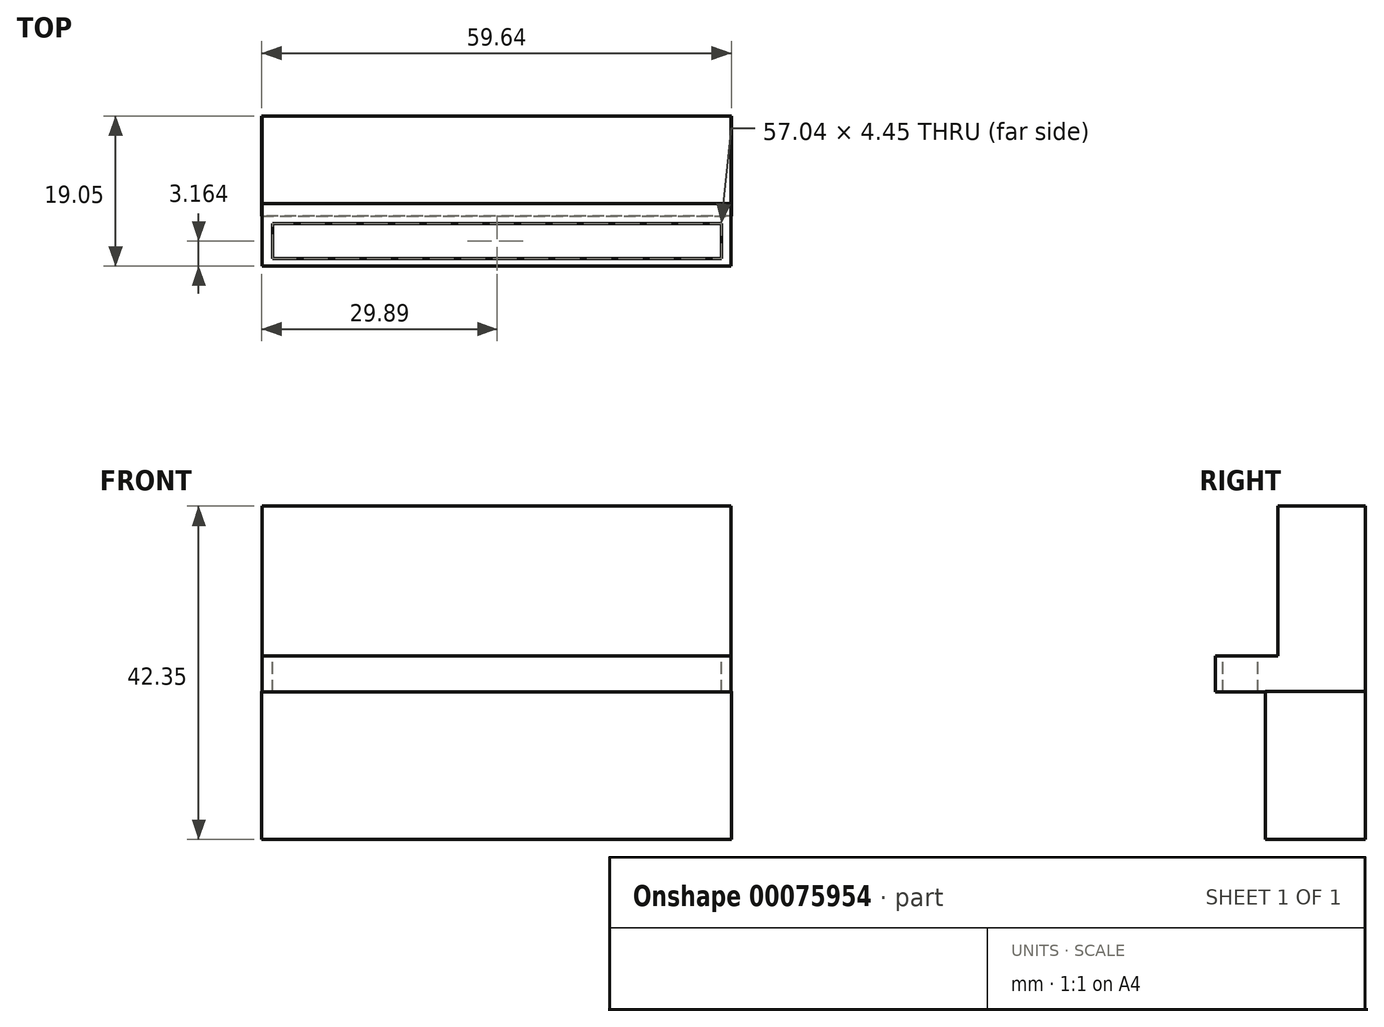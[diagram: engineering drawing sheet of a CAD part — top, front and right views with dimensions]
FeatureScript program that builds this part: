
annotation { "Feature Type Name" : "Feature", "Feature Type Description" : "" }
export const myFeature = defineFeature(function(context is Context, id is Id, definition is map)
    precondition{}
    {
        {
            var Q0;
            Q0=qCreatedBy(makeId("Front.planeOp"),FACE);
            var sketch = newSketch(context, id + "F0", { "sketchPlane" : qUnion([Q0])});
            skLineSegment(sketch, "E0.bottom", {"start": v(-27.17, 0) * mm, "end": v(32.47, 0) * mm});
            skLineSegment(sketch, "E0.top", {"start": v(-27.17, 18.8) * mm, "end": v(32.47, 18.8) * mm});
            skLineSegment(sketch, "E0.left", {"start": v(-27.17, 0) * mm, "end": v(-27.17, 18.8) * mm});
            skLineSegment(sketch, "E0.right", {"start": v(32.47, 0) * mm, "end": v(32.47, 18.8) * mm});
            skSolve(sketch);
        }
        {
            var Q0;
            Q0=makeQuery(id+"F0.imprint","IMPRINT",FACE,{"disambiguationData":[TD([[makeQuery(id+"F0.imprint","IMPRINT",EDGE,{"derivedFrom":sQuery(id+"F0.wireOp",EDGE,"E0.bottom")}),1.0]])]});
            extrude(context, id + "F1", {"entities" : qUnion([Q0]), "depth" : 12.7 * mm});
        }
        {
            var Q0;
            Q0=qCreatedBy(makeId("Front.planeOp"),FACE);
            var sketch = newSketch(context, id + "F2", { "sketchPlane" : qUnion([Q0])});
            skLineSegment(sketch, "E1.bottom", {"start": v(-27.1, 18.76) * mm, "end": v(32.42, 18.76) * mm});
            skLineSegment(sketch, "E1.top", {"start": v(-27.1, 23.3) * mm, "end": v(32.42, 23.3) * mm});
            skLineSegment(sketch, "E1.left", {"start": v(-27.1, 18.76) * mm, "end": v(-27.1, 23.3) * mm});
            skLineSegment(sketch, "E1.right", {"start": v(32.42, 18.76) * mm, "end": v(32.42, 23.3) * mm});
            skSolve(sketch);
        }
        {
            var Q0;
            Q0=makeQuery(id+"F2.imprint","IMPRINT",FACE,{"disambiguationData":[TD([[makeQuery(id+"F2.imprint","IMPRINT",EDGE,{"derivedFrom":sQuery(id+"F2.wireOp",EDGE,"E1.bottom")}),1.0]])]});
            extrude(context, id + "F3", {"entities" : qUnion([Q0]), "operationType" : NewBodyOperationType.ADD, "depth" : 19.05 * mm});
        }
        {
            var Q0;
            Q0=makeQuery(id+"F3.opExtrude","SWEPT_FACE",FACE,{"disambiguationData":[OSD([sQuery(id+"F2.wireOp",EDGE,"E1.top")])]});
            var sketch = newSketch(context, id + "F4", { "sketchPlane" : qUnion([Q0])});
            skLineSegment(sketch, "E2.bottom", {"start": v(-27.1, 0) * mm, "end": v(32.42, 0) * mm});
            skLineSegment(sketch, "E2.top", {"start": v(-27.1, -11.13) * mm, "end": v(32.42, -11.13) * mm});
            skLineSegment(sketch, "E2.left", {"start": v(-27.1, 0) * mm, "end": v(-27.1, -11.13) * mm});
            skLineSegment(sketch, "E2.right", {"start": v(32.42, 0) * mm, "end": v(32.42, -11.13) * mm});
            skSolve(sketch);
        }
        {
            var Q0;
            Q0=makeQuery(id+"F4.imprint","IMPRINT",FACE,{"disambiguationData":[TD([[makeQuery(id+"F4.imprint","IMPRINT",EDGE,{"derivedFrom":sQuery(id+"F4.wireOp",EDGE,"E2.bottom")}),-1.0]])]});
            extrude(context, id + "F5", {"entities" : qUnion([Q0]), "operationType" : NewBodyOperationType.ADD, "depth" : 19.05 * mm});
        }
        {
            var Q0;
            Q0=makeQuery(id+"F3.opExtrude","SWEPT_FACE",FACE,{"disambiguationData":[OSD([sQuery(id+"F2.wireOp",EDGE,"E1.top")])]});
            var sketch = newSketch(context, id + "F6", { "sketchPlane" : qUnion([Q0])});
            skLineSegment(sketch, "E3", {"start": v(32.42, -13.59) * mm, "end": v(-27.1, -13.59) * mm});
            skLineSegment(sketch, "E4", {"start": v(32.42, -13.59) * mm, "end": v(32.42, -11.13) * mm});
            skLineSegment(sketch, "E5", {"start": v(32.42, -11.13) * mm, "end": v(-27.1, -11.13) * mm});
            skLineSegment(sketch, "E6", {"start": v(-27.1, -11.13) * mm, "end": v(-27.1, -13.59) * mm});
            skSolve(sketch);
        }
        {
            var Q0;
            {var subQ0=sQuery(id+"F6.wireOp",EDGE,"E3");Q0=makeQuery(id+"F6.imprint","IMPRINT",FACE,{"disambiguationData":[TD([[makeQuery(id+"F6.imprint","IMPRINT",EDGE,{"derivedFrom":subQ0}),1.0]])]});}
            var sketch = newSketch(context, id + "F7", { "sketchPlane" : qUnion([Q0])});
            skLineSegment(sketch, "E7.bottom", {"start": v(-25.8, -13.66) * mm, "end": v(31.24, -13.66) * mm});
            skLineSegment(sketch, "E7.top", {"start": v(-25.8, -18.11) * mm, "end": v(31.24, -18.11) * mm});
            skLineSegment(sketch, "E7.left", {"start": v(-25.8, -13.66) * mm, "end": v(-25.8, -18.11) * mm});
            skLineSegment(sketch, "E7.right", {"start": v(31.24, -13.66) * mm, "end": v(31.24, -18.11) * mm});
            skSolve(sketch);
        }
        {
            var Q0;
            Q0=makeQuery(id+"F7.imprint","IMPRINT",FACE,{"disambiguationData":[TD([[makeQuery(id+"F7.imprint","IMPRINT",EDGE,{"derivedFrom":sQuery(id+"F7.wireOp",EDGE,"E7.bottom")}),-1.0]])]});
            extrude(context, id + "F8", {"entities" : qUnion([Q0]), "operationType" : NewBodyOperationType.REMOVE, "oppositeDirection" : true, "depth" : 12.7 * mm});
        }
    });
